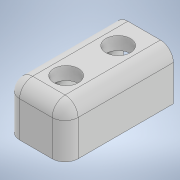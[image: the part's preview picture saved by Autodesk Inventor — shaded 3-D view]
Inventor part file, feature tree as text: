
AUTODESK INVENTOR PART (.ipt)
format: ipt  version: 2021 (Build 250183000, 183)  size: 393,216 bytes
history: native  units: in
note: dims shown in document units (in); Inventor stores cm internally (conversion verified against a paired STEP export)
features: extrude x6, sketch x3, fillet x2, other x2, imported_body x1
ambient origin geometry x8: Origin, YZ Plane, XZ Plane, XY Plane, X Axis, Y Axis, Z Axis, Center Point
bodies: Body1 (feature_tree)
feature tree (14):
  extrude  "Extrusion2"  Depth=2.126in
  extrude  "Extrusion3"  Depth=1.7717in
  extrude  "Extrusion4"  Depth=0.1969in
  fillet  "Fillet1"  Radius=1.122in
  extrude  "Extrusion5"  Depth=1.8898in
  fillet  "Fillet2"  Radius=1.8898in
  extrude  "Half"  Depth=1.8898in
  extrude  "Extrusion7"  Depth=0.1969in TaperAngle=0.0deg
  imported_body  "Base"
  other  "Top"
  other  "Walls"
  sketch  "Sketch7"  dims[d6=7.874in d7=2.126in]
  sketch  "Sketch10"  dims[d8=1.7717in d9=0.0in d10=1.122in]
  sketch  "Sketch13"  dims[d11=1.122in d12=1.122in d13=1.122in d14=1.8898in d15=1.8898in d16=1.8898in d19=0.7087in d20=0.0in d21=0.315in d22=0.315in d23=0.315in d24=0.315in d25=1.2992in d26=0.0in d27=0.8976in d28=0.8976in d29=0.8976in d30=0.8976in d31=0.9449in d32=3.937in d33=1.4961in d35=1.1024in d36=0.4724in d38=0.3937in d39=0.0in d40=0.2362in d41=0.1969in d44=3.937in d45=0.0in d50=0.1575in d52=0.315in d53=0.0in d54=0.315in d55=0.1969in d56=0.0in d46=0.0197in d47=0.0344in d48=0.0197in d49=0.0344in]
